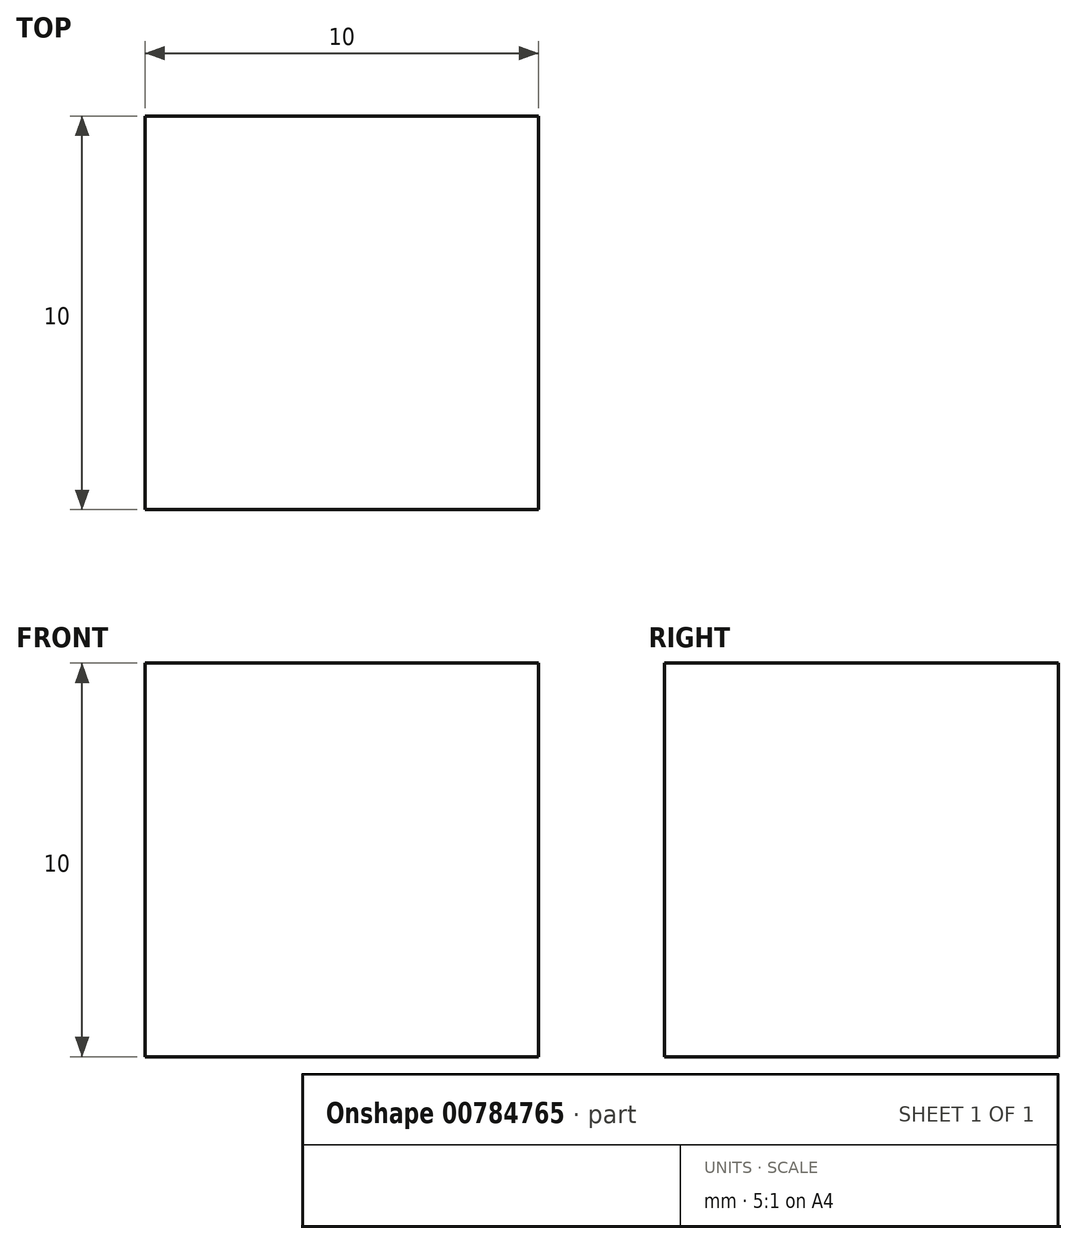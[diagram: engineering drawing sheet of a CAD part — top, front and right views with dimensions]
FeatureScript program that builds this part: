
annotation { "Feature Type Name" : "Feature", "Feature Type Description" : "" }
export const myFeature = defineFeature(function(context is Context, id is Id, definition is map)
    precondition{}
    {
        {
            var Q0;
            Q0=qCreatedBy(makeId("Top.planeOp"),FACE);
            var sketch = newSketch(context, id + "F0", { "sketchPlane" : qUnion([Q0])});
            skLineSegment(sketch, "E0.bottom", {"start": v(5, 5) * mm, "end": v(-5, 5) * mm});
            skLineSegment(sketch, "E0.top", {"start": v(5, -5) * mm, "end": v(-5, -5) * mm});
            skLineSegment(sketch, "E0.left", {"start": v(5, 5) * mm, "end": v(5, -5) * mm});
            skLineSegment(sketch, "E0.right", {"start": v(-5, 5) * mm, "end": v(-5, -5) * mm});
            skPoint(sketch, "E0.middle", {"position": v(0, 0) * mm});
            skSolve(sketch);
        }
        {
            var Q0;
            Q0=qSketchRegion(id+"F0",true);
            extrude(context, id + "F1", {"entities" : qUnion([Q0]), "depth" : 10 * mm, "offsetDistance" : 25 * mm});
        }
    });
